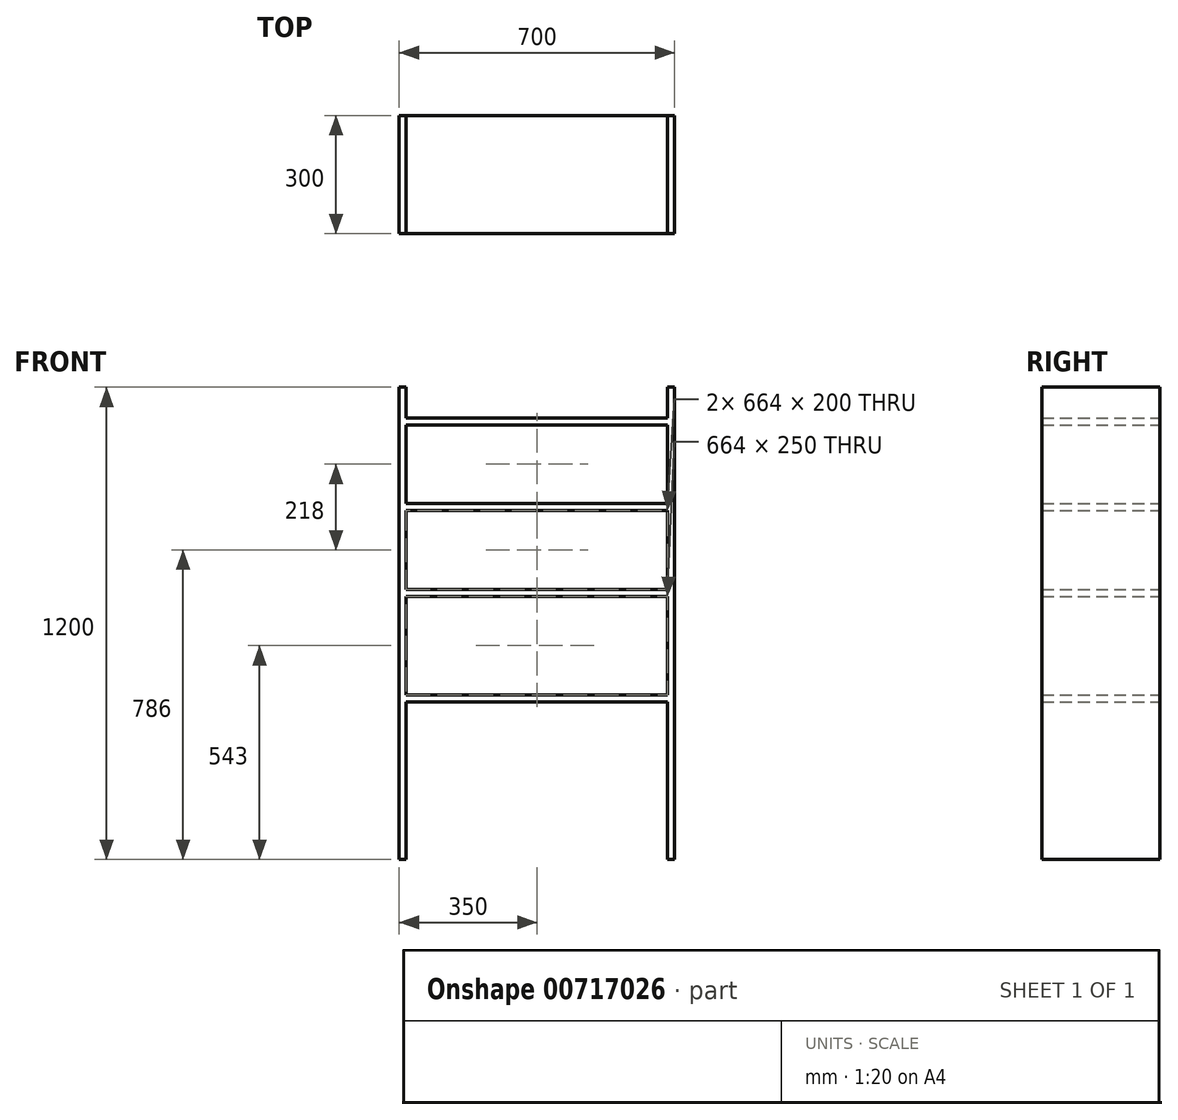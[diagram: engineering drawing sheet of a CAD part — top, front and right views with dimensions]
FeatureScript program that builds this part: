
annotation { "Feature Type Name" : "Feature", "Feature Type Description" : "" }
export const myFeature = defineFeature(function(context is Context, id is Id, definition is map)
    precondition{}
    {
        {
            var Q0;
            Q0=qCreatedBy(makeId("Front.planeOp"),FACE);
            var sketch = newSketch(context, id + "F0", { "sketchPlane" : qUnion([Q0])});
            skLineSegment(sketch, "E0.bottom", {"start": v(0, 0) * mm, "end": v(18, 0) * mm});
            skLineSegment(sketch, "E0.top", {"start": v(0, 1200) * mm, "end": v(18, 1200) * mm});
            skLineSegment(sketch, "E0.left", {"start": v(0, 0) * mm, "end": v(0, 1200) * mm});
            skLineSegment(sketch, "E0.right", {"start": v(18, 0) * mm, "end": v(18, 400) * mm});
            skLineSegment(sketch, "E1.bottom", {"start": v(682, 0) * mm, "end": v(700, 0) * mm});
            skLineSegment(sketch, "E1.top", {"start": v(682, 1200) * mm, "end": v(700, 1200) * mm});
            skLineSegment(sketch, "E1.left", {"start": v(682, 0) * mm, "end": v(682, 400) * mm});
            skLineSegment(sketch, "E1.right", {"start": v(700, 0) * mm, "end": v(700, 1200) * mm});
            skLineSegment(sketch, "E2.bottom", {"start": v(18, 418) * mm, "end": v(682, 418) * mm});
            skLineSegment(sketch, "E2.top", {"start": v(18, 400) * mm, "end": v(682, 400) * mm});
            skLineSegment(sketch, "E3.bottom", {"start": v(18, 668) * mm, "end": v(682, 668) * mm});
            skLineSegment(sketch, "E3.top", {"start": v(18, 686) * mm, "end": v(682, 686) * mm});
            skLineSegment(sketch, "E4.bottom", {"start": v(18, 886) * mm, "end": v(682, 886) * mm});
            skLineSegment(sketch, "E4.top", {"start": v(18, 904) * mm, "end": v(682, 904) * mm});
            skLineSegment(sketch, "E5.bottom", {"start": v(18, 1104) * mm, "end": v(682, 1104) * mm});
            skLineSegment(sketch, "E5.top", {"start": v(18, 1122) * mm, "end": v(682, 1122) * mm});
            skLineSegment(sketch, "E6.trimOffspring", {"start": v(18, 1122) * mm, "end": v(18, 1182) * mm});
            skLineSegment(sketch, "E7.trimOffspring", {"start": v(682, 1122) * mm, "end": v(682, 1182) * mm});
            skLineSegment(sketch, "E8.trimOffspring", {"start": v(18, 904) * mm, "end": v(18, 1104) * mm});
            skLineSegment(sketch, "E9.trimOffspring", {"start": v(682, 904) * mm, "end": v(682, 1104) * mm});
            skLineSegment(sketch, "E10.trimOffspring", {"start": v(18, 686) * mm, "end": v(18, 886) * mm});
            skLineSegment(sketch, "E11.trimOffspring", {"start": v(682, 686) * mm, "end": v(682, 886) * mm});
            skLineSegment(sketch, "E12.trimOffspring", {"start": v(682, 418) * mm, "end": v(682, 668) * mm});
            skLineSegment(sketch, "E13.trimOffspring", {"start": v(18, 418) * mm, "end": v(18, 668) * mm});
            skLineSegment(sketch, "E14", {"start": v(18, 1200) * mm, "end": v(18, 1182) * mm});
            skLineSegment(sketch, "E15", {"start": v(682, 1200) * mm, "end": v(682, 1182) * mm});
            skSolve(sketch);
        }
        {
            var Q0;
            Q0=makeQuery(id+"F0.imprint","IMPRINT",FACE,{"disambiguationData":[TD([[makeQuery(id+"F0.imprint","IMPRINT",EDGE,{"derivedFrom":sQuery(id+"F0.wireOp",EDGE,"E0.bottom")}),1.0]])]});
            extrude(context, id + "F1", {"entities" : qUnion([Q0]), "depth" : 300 * mm, "offsetDistance" : 25 * mm});
        }
    });
